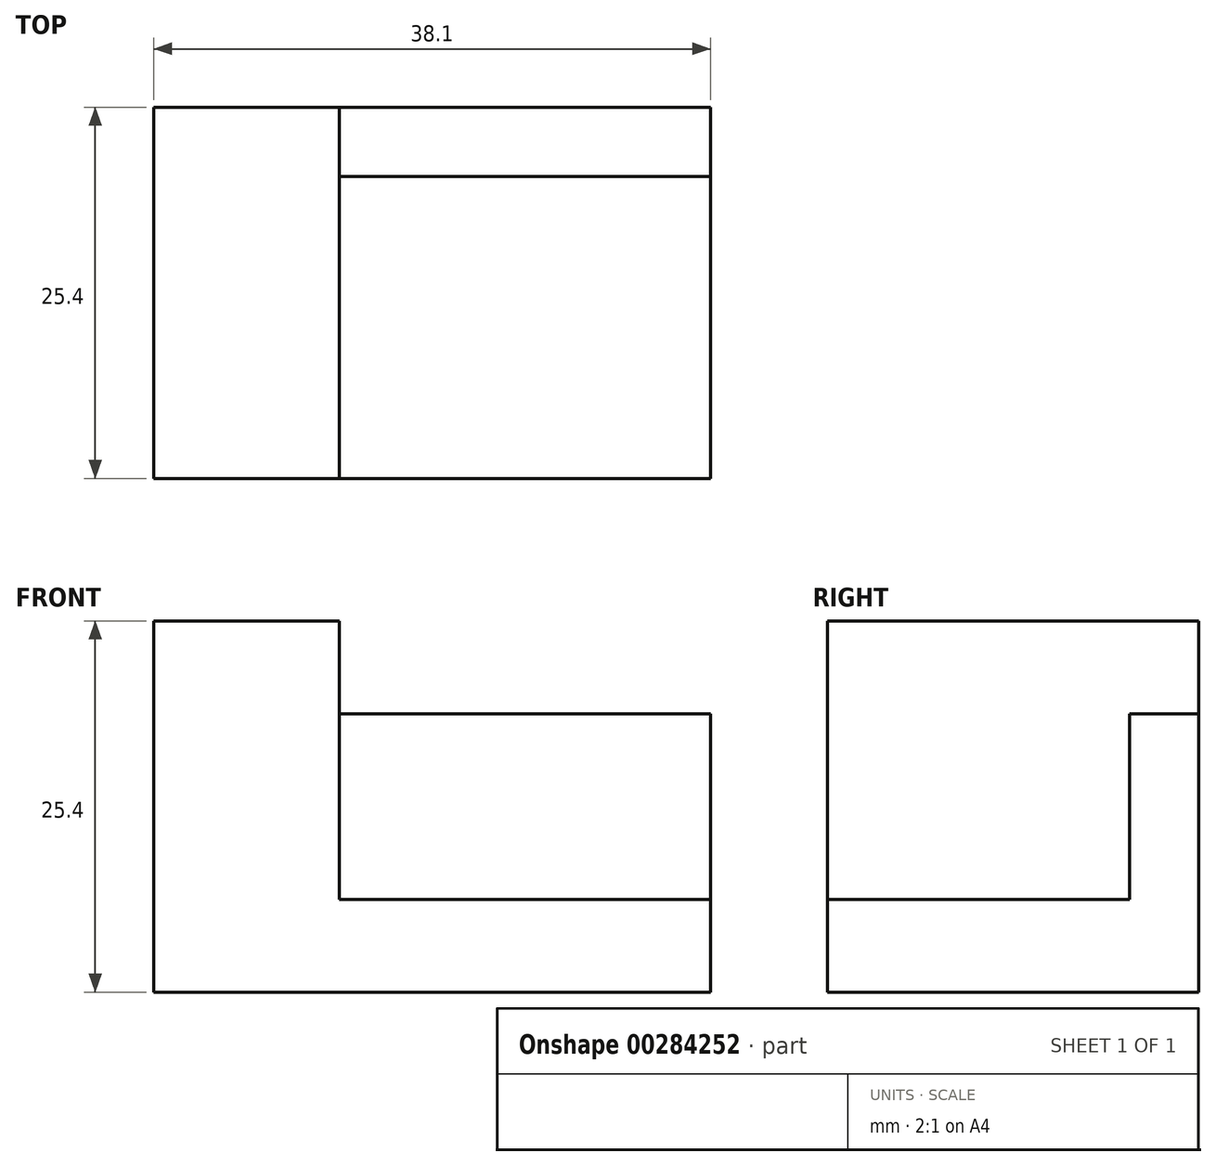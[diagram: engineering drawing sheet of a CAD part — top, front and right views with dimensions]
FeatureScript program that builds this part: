
annotation { "Feature Type Name" : "Feature", "Feature Type Description" : "" }
export const myFeature = defineFeature(function(context is Context, id is Id, definition is map)
    precondition{}
    {
        {
            var Q0;
            Q0=qCreatedBy(makeId("Front.planeOp"),FACE);
            var sketch = newSketch(context, id + "F0", { "sketchPlane" : qUnion([Q0])});
            skLineSegment(sketch, "E0", {"start": v(0, 0) * mm, "end": v(0, 25.4) * mm});
            skLineSegment(sketch, "E1", {"start": v(0, 25.4) * mm, "end": v(12.7, 25.4) * mm});
            skLineSegment(sketch, "E2", {"start": v(12.7, 25.4) * mm, "end": v(12.7, 6.35) * mm});
            skLineSegment(sketch, "E3", {"start": v(12.7, 6.35) * mm, "end": v(38.1, 6.35) * mm});
            skLineSegment(sketch, "E4", {"start": v(38.1, 6.35) * mm, "end": v(38.1, 0) * mm});
            skLineSegment(sketch, "E5", {"start": v(38.1, 0) * mm, "end": v(0, 0) * mm});
            skSolve(sketch);
        }
        {
            var Q0;
            Q0=makeQuery(id+"F0.imprint","IMPRINT",FACE,{"disambiguationData":[TD([[makeQuery(id+"F0.imprint","IMPRINT",EDGE,{"derivedFrom":sQuery(id+"F0.wireOp",EDGE,"E0")}),-1.0]])]});
            extrude(context, id + "F1", {"entities" : qUnion([Q0]), "depth" : 25.4 * mm});
        }
        {
            var Q0;
            Q0=makeQuery(id+"F1.opExtrude","SWEPT_FACE",FACE,{"disambiguationData":[OSD([sQuery(id+"F0.wireOp",EDGE,"E2")])]});
            var sketch = newSketch(context, id + "F2", { "sketchPlane" : qUnion([Q0])});
            skLineSegment(sketch, "E6", {"start": v(-4.74, 19.05) * mm, "end": v(-4.74, 6.35) * mm});
            skLineSegment(sketch, "E7", {"start": v(-4.74, 19.05) * mm, "end": v(0, 19.05) * mm});
            skLineSegment(sketch, "E8", {"start": v(0, 19.05) * mm, "end": v(0, 6.35) * mm});
            skLineSegment(sketch, "E9", {"start": v(0, 6.35) * mm, "end": v(-4.74, 6.35) * mm});
            skSolve(sketch);
        }
        {
            var Q0;
            Q0=makeQuery(id+"F2.imprint","IMPRINT",FACE,{"disambiguationData":[TD([[makeQuery(id+"F2.imprint","IMPRINT",EDGE,{"derivedFrom":sQuery(id+"F2.wireOp",EDGE,"E6")}),1.0]])]});
            extrude(context, id + "F3", {"entities" : qUnion([Q0]), "operationType" : NewBodyOperationType.ADD, "depth" : 25.4 * mm});
        }
    });
